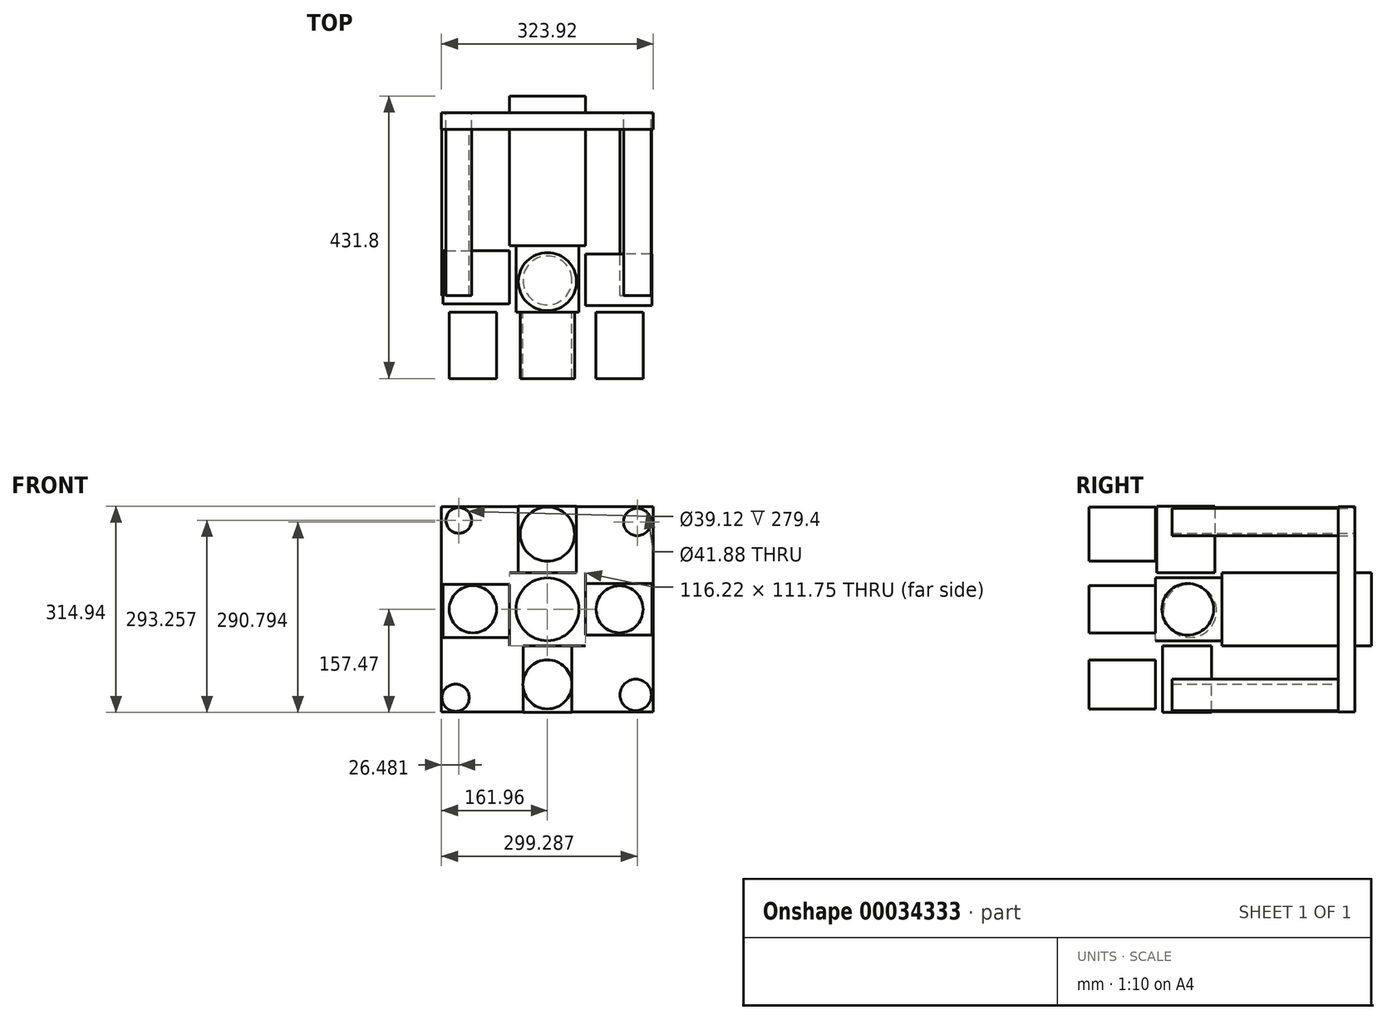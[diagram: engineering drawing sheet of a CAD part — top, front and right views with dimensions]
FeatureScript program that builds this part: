
annotation { "Feature Type Name" : "Feature", "Feature Type Description" : "" }
export const myFeature = defineFeature(function(context is Context, id is Id, definition is map)
    precondition{}
    {
        {
            var Q0;
            Q0=qCreatedBy(makeId("Front.planeOp"),FACE);
            var sketch = newSketch(context, id + "F0", { "sketchPlane" : qUnion([Q0])});
            skLineSegment(sketch, "E0.rect.bottom", {"start": v(58.7, -59.15) * mm, "end": v(-58.7, -59.15) * mm});
            skLineSegment(sketch, "E0.rect.top", {"start": v(58.7, 59.15) * mm, "end": v(-58.7, 59.15) * mm});
            skLineSegment(sketch, "E0.rect.left", {"start": v(58.7, -59.15) * mm, "end": v(58.7, 59.15) * mm});
            skLineSegment(sketch, "E0.rect.right", {"start": v(-58.7, -59.15) * mm, "end": v(-58.7, 59.15) * mm});
            skPoint(sketch, "E0.rect.middle", {"position": v(0, 0) * mm});
            skSolve(sketch);
        }
        {
            var Q0;
            Q0=makeQuery(id+"F0.imprint","IMPRINT",FACE,{"disambiguationData":[TD([[makeQuery(id+"F0.imprint","IMPRINT",EDGE,{"derivedFrom":sQuery(id+"F0.wireOp",EDGE,"E0.rect.bottom")}),-1.0]])]});
            extrude(context, id + "F1", {"entities" : qUnion([Q0]), "depth" : 50.8 * mm});
        }
        {
            var Q0;
            Q0=makeQuery(id+"F1.opExtrude","CAP_FACE",FACE,{"disambiguationData":[OSD([sQuery(id+"F0.wireOp",EDGE,"E0.rect.bottom"),sQuery(id+"F0.wireOp",EDGE,"E0.rect.top"),sQuery(id+"F0.wireOp",EDGE,"E0.rect.left"),sQuery(id+"F0.wireOp",EDGE,"E0.rect.right")])],"isStart":true});
            var sketch = newSketch(context, id + "F2", { "sketchPlane" : qUnion([Q0])});
            skCircle(sketch, "E1", {"center": v(0, 0) * mm, "radius": 46.9 * mm});
            skSolve(sketch);
        }
        {
            var Q0;
            Q0=makeQuery(id+"F2.imprint","IMPRINT",FACE,{"disambiguationData":[TD([[makeQuery(id+"F2.imprint","IMPRINT",EDGE,{"derivedFrom":sQuery(id+"F2.wireOp",EDGE,"E1")}),1.0]])]});
            extrude(context, id + "F3", {"entities" : qUnion([Q0]), "operationType" : NewBodyOperationType.ADD, "oppositeDirection" : true, "depth" : 50.8 * mm});
        }
        {
            var Q0;
            Q0=makeQuery(id+"F1.opExtrude","CAP_FACE",FACE,{"disambiguationData":[OSD([sQuery(id+"F0.wireOp",EDGE,"E0.rect.bottom"),sQuery(id+"F0.wireOp",EDGE,"E0.rect.top"),sQuery(id+"F0.wireOp",EDGE,"E0.rect.left"),sQuery(id+"F0.wireOp",EDGE,"E0.rect.right")])],"isStart":false});
            var sketch = newSketch(context, id + "F4", { "sketchPlane" : qUnion([Q0])});
            skCircle(sketch, "E2", {"center": v(0, 0) * mm, "radius": 42.26 * mm});
            skSolve(sketch);
        }
        {
            var Q0;
            Q0=makeQuery(id+"F4.imprint","IMPRINT",FACE,{"disambiguationData":[TD([[makeQuery(id+"F4.imprint","IMPRINT",EDGE,{"derivedFrom":sQuery(id+"F4.wireOp",EDGE,"E2")}),1.0]])]});
            extrude(context, id + "F5", {"entities" : qUnion([Q0]), "operationType" : NewBodyOperationType.ADD, "depth" : 50.8 * mm});
        }
        {
            var Q0;
            Q0=makeQuery(id+"F1.opExtrude","SWEPT_BODY",BODY,{"disambiguationData":[OSD([sQuery(id+"F0.wireOp",EDGE,"E0.rect.bottom"),sQuery(id+"F0.wireOp",EDGE,"E0.rect.top"),sQuery(id+"F0.wireOp",EDGE,"E0.rect.left"),sQuery(id+"F0.wireOp",EDGE,"E0.rect.right")])]});
            deleteBodies(context, id + "F6", {"entities" : qUnion([Q0])});
        }
        {
            var Q0;
            Q0=qCreatedBy(makeId("Front.planeOp"),FACE);
            var sketch = newSketch(context, id + "F7", { "sketchPlane" : qUnion([Q0])});
            skLineSegment(sketch, "E3.rect.bottom", {"start": v(27.41, -56.77) * mm, "end": v(-27.41, -56.77) * mm});
            skLineSegment(sketch, "E3.rect.top", {"start": v(27.41, 56.77) * mm, "end": v(-27.41, 56.77) * mm});
            skLineSegment(sketch, "E3.rect.left", {"start": v(27.41, -56.77) * mm, "end": v(27.41, 56.77) * mm});
            skLineSegment(sketch, "E3.rect.right", {"start": v(-27.41, -56.77) * mm, "end": v(-27.41, 56.77) * mm});
            skPoint(sketch, "E3.rect.middle", {"position": v(0, 0) * mm});
            skSolve(sketch);
        }
        {
            var Q0;
            Q0=makeQuery(id+"F7.imprint","IMPRINT",FACE,{"disambiguationData":[TD([[makeQuery(id+"F7.imprint","IMPRINT",EDGE,{"derivedFrom":sQuery(id+"F7.wireOp",EDGE,"E3.rect.bottom")}),-1.0]])]});
            extrude(context, id + "F8", {"entities" : qUnion([Q0]), "depth" : 50.8 * mm});
        }
        {
            var Q0;
            Q0=makeQuery(id+"F8.opExtrude","SWEPT_FACE",FACE,{"disambiguationData":[OSD([sQuery(id+"F7.wireOp",EDGE,"E3.rect.left")])]});
            var sketch = newSketch(context, id + "F9", { "sketchPlane" : qUnion([Q0])});
            skSolve(sketch);
        }
        {
            var Q0;
            {var subQ0=sQuery(id+"F7.wireOp",EDGE,"E3.rect.left");Q0=makeQuery(id+"F9.imprint","IMPRINT",FACE,{"disambiguationData":[TD([[makeQuery(id+"F9.imprint","IMPRINT",EDGE,{"derivedFrom":makeQuery(id+"F8.opExtrude","CAP_EDGE",EDGE,{"disambiguationData":[OSD([subQ0])],"isStart":true})}),1.0]])]});}
            extrude(context, id + "F10", {"entities" : qUnion([Q0]), "operationType" : NewBodyOperationType.ADD, "depth" : 25.4 * mm});
        }
        {
            var Q0;
            Q0=makeQuery(id+"F8.opExtrude","SWEPT_BODY",BODY,{"disambiguationData":[OSD([sQuery(id+"F7.wireOp",EDGE,"E3.rect.bottom"),sQuery(id+"F7.wireOp",EDGE,"E3.rect.top"),sQuery(id+"F7.wireOp",EDGE,"E3.rect.left"),sQuery(id+"F7.wireOp",EDGE,"E3.rect.right")])]});
            deleteBodies(context, id + "F11", {"entities" : qUnion([Q0])});
        }
        {
            var Q0;
            Q0=qCreatedBy(makeId("Front.planeOp"),FACE);
            var sketch = newSketch(context, id + "F12", { "sketchPlane" : qUnion([Q0])});
            skLineSegment(sketch, "E4.rect.bottom", {"start": v(58.1, -55.87) * mm, "end": v(-58.1, -55.87) * mm});
            skLineSegment(sketch, "E4.rect.top", {"start": v(58.1, 55.87) * mm, "end": v(-58.1, 55.87) * mm});
            skLineSegment(sketch, "E4.rect.left", {"start": v(58.1, -55.87) * mm, "end": v(58.1, 55.87) * mm});
            skLineSegment(sketch, "E4.rect.right", {"start": v(-58.1, -55.87) * mm, "end": v(-58.1, 55.87) * mm});
            skPoint(sketch, "E4.rect.middle", {"position": v(0, 0) * mm});
            skSolve(sketch);
        }
        {
            var Q0;
            Q0=makeQuery(id+"F12.imprint","IMPRINT",FACE,{"disambiguationData":[TD([[makeQuery(id+"F12.imprint","IMPRINT",EDGE,{"derivedFrom":sQuery(id+"F12.wireOp",EDGE,"E4.rect.bottom")}),-1.0]])]});
            var sketch = newSketch(context, id + "F13", { "sketchPlane" : qUnion([Q0])});
            skCircle(sketch, "E5", {"center": v(0, 0) * mm, "radius": 40.06 * mm});
            skSolve(sketch);
        }
        {
            var Q0;
            Q0=makeQuery(id+"F12.imprint","IMPRINT",FACE,{"disambiguationData":[TD([[makeQuery(id+"F12.imprint","IMPRINT",EDGE,{"derivedFrom":sQuery(id+"F12.wireOp",EDGE,"E4.rect.bottom")}),-1.0]])]});
            extrude(context, id + "F14", {"entities" : qUnion([Q0]), "depth" : 101.6 * mm});
        }
        {
            var Q0;
            Q0=makeQuery(id+"F13.imprint","IMPRINT",FACE,{"disambiguationData":[TD([[makeQuery(id+"F13.imprint","IMPRINT",EDGE,{"derivedFrom":sQuery(id+"F13.wireOp",EDGE,"E5")}),1.0]])]});
            extrude(context, id + "F15", {"entities" : qUnion([Q0]), "operationType" : NewBodyOperationType.ADD, "depth" : 25.4 * mm});
        }
        {
            var Q0;
            Q0=makeQuery(id+"F14.opExtrude","CAP_FACE",FACE,{"disambiguationData":[OSD([sQuery(id+"F12.wireOp",EDGE,"E4.rect.bottom"),sQuery(id+"F12.wireOp",EDGE,"E4.rect.top"),sQuery(id+"F12.wireOp",EDGE,"E4.rect.left"),sQuery(id+"F12.wireOp",EDGE,"E4.rect.right")])],"isStart":false});
            var sketch = newSketch(context, id + "F16", { "sketchPlane" : qUnion([Q0])});
            skCircle(sketch, "E6", {"center": v(0, 0) * mm, "radius": 48.05 * mm});
            skSolve(sketch);
        }
        {
            var Q0;
            Q0=makeQuery(id+"F16.imprint","IMPRINT",FACE,{"disambiguationData":[TD([[makeQuery(id+"F16.imprint","IMPRINT",EDGE,{"derivedFrom":sQuery(id+"F16.wireOp",EDGE,"E6")}),1.0]])]});
            extrude(context, id + "F17", {"entities" : qUnion([Q0]), "operationType" : NewBodyOperationType.ADD, "depth" : 101.6 * mm});
        }
        {
            var Q0;
            Q0=makeQuery(id+"F14.opExtrude","SWEPT_FACE",FACE,{"disambiguationData":[OSD([sQuery(id+"F12.wireOp",EDGE,"E4.rect.right")])]});
            var sketch = newSketch(context, id + "F18", { "sketchPlane" : qUnion([Q0])});
            skCircle(sketch, "E7", {"center": v(150.17, -2.53) * mm, "radius": 40.58 * mm});
            skSolve(sketch);
        }
        {
            var Q0;
            Q0=makeQuery(id+"F18.imprint","IMPRINT",FACE,{"disambiguationData":[TD([[makeQuery(id+"F18.imprint","IMPRINT",EDGE,{"derivedFrom":sQuery(id+"F18.wireOp",EDGE,"E7")}),1.0]])]});
            extrude(context, id + "F19", {"entities" : qUnion([Q0]), "depth" : 101.6 * mm});
        }
        {
            var Q0;
            Q0=makeQuery(id+"F14.opExtrude","SWEPT_FACE",FACE,{"disambiguationData":[OSD([sQuery(id+"F12.wireOp",EDGE,"E4.rect.top")])]});
            var sketch = newSketch(context, id + "F20", { "sketchPlane" : qUnion([Q0])});
            skCircle(sketch, "E8", {"center": v(0, -156.63) * mm, "radius": 44.41 * mm});
            skSolve(sketch);
        }
        {
            var Q0;
            Q0=makeQuery(id+"F20.imprint","IMPRINT",FACE,{"disambiguationData":[TD([[makeQuery(id+"F20.imprint","IMPRINT",EDGE,{"derivedFrom":sQuery(id+"F20.wireOp",EDGE,"E8")}),1.0]])]});
            extrude(context, id + "F21", {"entities" : qUnion([Q0]), "depth" : 101.6 * mm});
        }
        {
            var Q0;
            Q0=makeQuery(id+"F14.opExtrude","SWEPT_FACE",FACE,{"disambiguationData":[OSD([sQuery(id+"F12.wireOp",EDGE,"E4.rect.left")])]});
            var sketch = newSketch(context, id + "F22", { "sketchPlane" : qUnion([Q0])});
            skCircle(sketch, "E9", {"center": v(-153.69, 0) * mm, "radius": 39.5 * mm});
            skSolve(sketch);
        }
        {
            var Q0;
            Q0=makeQuery(id+"F22.imprint","IMPRINT",FACE,{"disambiguationData":[TD([[makeQuery(id+"F22.imprint","IMPRINT",EDGE,{"derivedFrom":sQuery(id+"F22.wireOp",EDGE,"E9")}),1.0]])]});
            extrude(context, id + "F23", {"entities" : qUnion([Q0]), "depth" : 101.6 * mm});
        }
        {
            var Q0;
            Q0=makeQuery(id+"F14.opExtrude","SWEPT_FACE",FACE,{"disambiguationData":[OSD([sQuery(id+"F12.wireOp",EDGE,"E4.rect.bottom")])]});
            var sketch = newSketch(context, id + "F24", { "sketchPlane" : qUnion([Q0])});
            skCircle(sketch, "E10", {"center": v(0, 154.64) * mm, "radius": 37.4 * mm});
            skSolve(sketch);
        }
        {
            var Q0;
            Q0=makeQuery(id+"F24.imprint","IMPRINT",FACE,{"disambiguationData":[TD([[makeQuery(id+"F24.imprint","IMPRINT",EDGE,{"derivedFrom":sQuery(id+"F24.wireOp",EDGE,"E10")}),1.0]])]});
            extrude(context, id + "F25", {"entities" : qUnion([Q0]), "depth" : 101.6 * mm});
        }
        {
            var Q0;
            Q0=makeQuery(id+"F14.opExtrude","CAP_FACE",FACE,{"disambiguationData":[OSD([sQuery(id+"F12.wireOp",EDGE,"E4.rect.bottom"),sQuery(id+"F12.wireOp",EDGE,"E4.rect.top"),sQuery(id+"F12.wireOp",EDGE,"E4.rect.left"),sQuery(id+"F12.wireOp",EDGE,"E4.rect.right")])],"isStart":true});
            var sketch = newSketch(context, id + "F26", { "sketchPlane" : qUnion([Q0])});
            skLineSegment(sketch, "E11.rect.bottom", {"start": v(58.1, -55.87) * mm, "end": v(-58.1, -55.87) * mm});
            skLineSegment(sketch, "E11.rect.top", {"start": v(58.1, 55.87) * mm, "end": v(-58.1, 55.87) * mm});
            skLineSegment(sketch, "E11.rect.left", {"start": v(58.1, -55.87) * mm, "end": v(58.1, 55.87) * mm});
            skLineSegment(sketch, "E11.rect.right", {"start": v(-58.1, -55.87) * mm, "end": v(-58.1, 55.87) * mm});
            skPoint(sketch, "E11.rect.middle", {"position": v(0, 0) * mm});
            skSolve(sketch);
        }
        {
            var Q0;
            Q0=makeQuery(id+"F26.imprint","IMPRINT",FACE,{"disambiguationData":[TD([[makeQuery(id+"F26.imprint","IMPRINT",EDGE,{"derivedFrom":sQuery(id+"F26.wireOp",EDGE,"E11.rect.bottom")}),1.0]])]});
            extrude(context, id + "F27", {"entities" : qUnion([Q0]), "operationType" : NewBodyOperationType.ADD, "depth" : 101.6 * mm});
        }
        {
            var Q0;
            Q0=makeQuery(id+"F17.opExtrude","CAP_FACE",FACE,{"disambiguationData":[OSD([sQuery(id+"F16.wireOp",EDGE,"E6")])],"isStart":false});
            var sketch = newSketch(context, id + "F28", { "sketchPlane" : qUnion([Q0])});
            skCircle(sketch, "E12", {"center": v(0, 114.85) * mm, "radius": 41.52 * mm});
            skSolve(sketch);
        }
        {
            var Q0;
            Q0=makeQuery(id+"F28.imprint","IMPRINT",FACE,{"disambiguationData":[TD([[makeQuery(id+"F28.imprint","IMPRINT",EDGE,{"derivedFrom":sQuery(id+"F28.wireOp",EDGE,"E12")}),1.0]])]});
            extrude(context, id + "F29", {"entities" : qUnion([Q0]), "depth" : 101.6 * mm});
        }
        {
            var Q0;
            Q0=makeQuery(id+"F17.opExtrude","CAP_FACE",FACE,{"disambiguationData":[OSD([sQuery(id+"F16.wireOp",EDGE,"E6")])],"isStart":false});
            var sketch = newSketch(context, id + "F30", { "sketchPlane" : qUnion([Q0])});
            skCircle(sketch, "E13", {"center": v(-113.93, 0) * mm, "radius": 36.08 * mm});
            skSolve(sketch);
        }
        {
            var Q0;
            Q0=makeQuery(id+"F30.imprint","IMPRINT",FACE,{"disambiguationData":[TD([[makeQuery(id+"F30.imprint","IMPRINT",EDGE,{"derivedFrom":sQuery(id+"F30.wireOp",EDGE,"E13")}),1.0]])]});
            extrude(context, id + "F31", {"entities" : qUnion([Q0]), "depth" : 101.6 * mm});
        }
        {
            var Q0;
            Q0=makeQuery(id+"F17.opExtrude","CAP_FACE",FACE,{"disambiguationData":[OSD([sQuery(id+"F16.wireOp",EDGE,"E6")])],"isStart":false});
            var sketch = newSketch(context, id + "F32", { "sketchPlane" : qUnion([Q0])});
            skCircle(sketch, "E14", {"center": v(110.23, 0) * mm, "radius": 35.93 * mm});
            skSolve(sketch);
        }
        {
            var Q0;
            Q0=makeQuery(id+"F32.imprint","IMPRINT",FACE,{"disambiguationData":[TD([[makeQuery(id+"F32.imprint","IMPRINT",EDGE,{"derivedFrom":sQuery(id+"F32.wireOp",EDGE,"E14")}),1.0]])]});
            extrude(context, id + "F33", {"entities" : qUnion([Q0]), "depth" : 101.6 * mm});
        }
        {
            var Q0;
            Q0=makeQuery(id+"F17.opExtrude","CAP_FACE",FACE,{"disambiguationData":[OSD([sQuery(id+"F16.wireOp",EDGE,"E6")])],"isStart":false});
            var sketch = newSketch(context, id + "F34", { "sketchPlane" : qUnion([Q0])});
            skCircle(sketch, "E15", {"center": v(0, -114.85) * mm, "radius": 37.46 * mm});
            skSolve(sketch);
        }
        {
            var Q0;
            Q0=makeQuery(id+"F34.imprint","IMPRINT",FACE,{"disambiguationData":[TD([[makeQuery(id+"F34.imprint","IMPRINT",EDGE,{"derivedFrom":sQuery(id+"F34.wireOp",EDGE,"E15")}),1.0]])]});
            extrude(context, id + "F35", {"entities" : qUnion([Q0]), "depth" : 101.6 * mm});
        }
        {
            var Q0;
            Q0=makeQuery(id+"F27.opExtrude","CAP_FACE",FACE,{"disambiguationData":[OSD([sQuery(id+"F26.wireOp",EDGE,"E11.rect.bottom"),sQuery(id+"F26.wireOp",EDGE,"E11.rect.top"),sQuery(id+"F26.wireOp",EDGE,"E11.rect.left"),sQuery(id+"F26.wireOp",EDGE,"E11.rect.right")])],"isStart":false});
            var sketch = newSketch(context, id + "F36", { "sketchPlane" : qUnion([Q0])});
            skLineSegment(sketch, "E16.rect.bottom", {"start": v(161.96, -156.73) * mm, "end": v(-161.96, -156.73) * mm});
            skLineSegment(sketch, "E16.rect.top", {"start": v(161.96, 156.73) * mm, "end": v(-161.96, 156.73) * mm});
            skLineSegment(sketch, "E16.rect.left", {"start": v(161.96, -156.73) * mm, "end": v(161.96, 156.73) * mm});
            skLineSegment(sketch, "E16.rect.right", {"start": v(-161.96, -156.73) * mm, "end": v(-161.96, 156.73) * mm});
            skPoint(sketch, "E16.rect.middle", {"position": v(0, 0) * mm});
            skSolve(sketch);
        }
        {
            var Q0;
            Q0=makeQuery(id+"F36.imprint","IMPRINT",FACE,{"disambiguationData":[TD([[makeQuery(id+"F36.imprint","IMPRINT",EDGE,{"derivedFrom":sQuery(id+"F36.wireOp",EDGE,"E16.rect.bottom")}),-1.0]])]});
            extrude(context, id + "F37", {"entities" : qUnion([Q0]), "depth" : 25.4 * mm});
        }
        {
            var Q0;
            Q0=makeQuery(id+"F27.opExtrude","CAP_FACE",FACE,{"disambiguationData":[OSD([sQuery(id+"F26.wireOp",EDGE,"E11.rect.bottom"),sQuery(id+"F26.wireOp",EDGE,"E11.rect.top"),sQuery(id+"F26.wireOp",EDGE,"E11.rect.left"),sQuery(id+"F26.wireOp",EDGE,"E11.rect.right")])],"isStart":false});
            var sketch = newSketch(context, id + "F38", { "sketchPlane" : qUnion([Q0])});
            skLineSegment(sketch, "E17.rect.bottom", {"start": v(58.1, -55.87) * mm, "end": v(-58.1, -55.87) * mm});
            skLineSegment(sketch, "E17.rect.top", {"start": v(58.1, 55.87) * mm, "end": v(-58.1, 55.87) * mm});
            skLineSegment(sketch, "E17.rect.left", {"start": v(58.1, -55.87) * mm, "end": v(58.1, 55.87) * mm});
            skLineSegment(sketch, "E17.rect.right", {"start": v(-58.1, -55.87) * mm, "end": v(-58.1, 55.87) * mm});
            skPoint(sketch, "E17.rect.middle", {"position": v(0, 0) * mm});
            skSolve(sketch);
        }
        {
            var Q0;
            Q0=makeQuery(id+"F38.imprint","IMPRINT",FACE,{"disambiguationData":[TD([[makeQuery(id+"F38.imprint","IMPRINT",EDGE,{"derivedFrom":sQuery(id+"F38.wireOp",EDGE,"E17.rect.bottom")}),1.0]])]});
            extrude(context, id + "F39", {"entities" : qUnion([Q0]), "depth" : 25.4 * mm});
        }
        {
            var Q0;
            Q0=makeQuery(id+"F37.opExtrude","CAP_FACE",FACE,{"disambiguationData":[OSD([sQuery(id+"F26.wireOp",EDGE,"E11.rect.bottom"),sQuery(id+"F26.wireOp",EDGE,"E11.rect.top"),sQuery(id+"F26.wireOp",EDGE,"E11.rect.left"),sQuery(id+"F26.wireOp",EDGE,"E11.rect.right"),sQuery(id+"F36.wireOp",EDGE,"E16.rect.bottom"),sQuery(id+"F36.wireOp",EDGE,"E16.rect.top"),sQuery(id+"F36.wireOp",EDGE,"E16.rect.left"),sQuery(id+"F36.wireOp",EDGE,"E16.rect.right")])],"isStart":true});
            var sketch = newSketch(context, id + "F40", { "sketchPlane" : qUnion([Q0])});
            skCircle(sketch, "E18", {"center": v(-135.48, 135.79) * mm, "radius": 19.56 * mm});
            skCircle(sketch, "E19", {"center": v(138.56, 136.4) * mm, "radius": 18.62 * mm});
            skCircle(sketch, "E20", {"center": v(134.25, -133.94) * mm, "radius": 23.12 * mm});
            skCircle(sketch, "E21", {"center": v(-133.02, -135.17) * mm, "radius": 20.66 * mm});
            skSolve(sketch);
        }
        {
            var Q0;
            Q0=makeQuery(id+"F40.imprint","IMPRINT",FACE,{"disambiguationData":[TD([[makeQuery(id+"F40.imprint","IMPRINT",EDGE,{"derivedFrom":sQuery(id+"F40.wireOp",EDGE,"E18")}),1.0]])]});
            extrude(context, id + "F41", {"entities" : qUnion([Q0]), "operationType" : NewBodyOperationType.ADD, "depth" : 254 * mm});
        }
        {
            var Q0;
            Q0=makeQuery(id+"F37.opExtrude","CAP_FACE",FACE,{"disambiguationData":[OSD([sQuery(id+"F26.wireOp",EDGE,"E11.rect.bottom"),sQuery(id+"F26.wireOp",EDGE,"E11.rect.top"),sQuery(id+"F26.wireOp",EDGE,"E11.rect.left"),sQuery(id+"F26.wireOp",EDGE,"E11.rect.right"),sQuery(id+"F36.wireOp",EDGE,"E16.rect.bottom"),sQuery(id+"F36.wireOp",EDGE,"E16.rect.top"),sQuery(id+"F36.wireOp",EDGE,"E16.rect.left"),sQuery(id+"F36.wireOp",EDGE,"E16.rect.right")])],"isStart":true});
            var sketch = newSketch(context, id + "F42", { "sketchPlane" : qUnion([Q0])});
            skCircle(sketch, "E22", {"center": v(137.33, 133.32) * mm, "radius": 20.94 * mm});
            skSolve(sketch);
        }
        {
            var Q0;
            Q0=makeQuery(id+"F37.opExtrude","SWEPT_BODY",BODY,{"disambiguationData":[OSD([sQuery(id+"F26.wireOp",EDGE,"E11.rect.bottom"),sQuery(id+"F26.wireOp",EDGE,"E11.rect.top"),sQuery(id+"F26.wireOp",EDGE,"E11.rect.left"),sQuery(id+"F26.wireOp",EDGE,"E11.rect.right"),sQuery(id+"F36.wireOp",EDGE,"E16.rect.bottom"),sQuery(id+"F36.wireOp",EDGE,"E16.rect.top"),sQuery(id+"F36.wireOp",EDGE,"E16.rect.left"),sQuery(id+"F36.wireOp",EDGE,"E16.rect.right")])]});
            deleteBodies(context, id + "F43", {"entities" : qUnion([Q0])});
        }
        {
            var Q0;
            Q0=makeQuery(id+"F42.imprint","IMPRINT",FACE,{"disambiguationData":[TD([[makeQuery(id+"F42.imprint","IMPRINT",EDGE,{"derivedFrom":sQuery(id+"F42.wireOp",EDGE,"E22")}),-1.0]])]});
            extrude(context, id + "F44", {"entities" : qUnion([Q0]), "operationType" : NewBodyOperationType.ADD, "depth" : 25.4 * mm});
        }
        {
            var Q0;
            Q0=makeQuery(id+"F44.opExtrude","CAP_FACE",FACE,{"disambiguationData":[OSD([sQuery(id+"F26.wireOp",EDGE,"E11.rect.bottom"),sQuery(id+"F26.wireOp",EDGE,"E11.rect.top"),sQuery(id+"F26.wireOp",EDGE,"E11.rect.left"),sQuery(id+"F26.wireOp",EDGE,"E11.rect.right"),sQuery(id+"F36.wireOp",EDGE,"E16.rect.bottom"),sQuery(id+"F36.wireOp",EDGE,"E16.rect.top"),sQuery(id+"F36.wireOp",EDGE,"E16.rect.left"),sQuery(id+"F36.wireOp",EDGE,"E16.rect.right"),sQuery(id+"F40.wireOp",EDGE,"E18"),sQuery(id+"F42.wireOp",EDGE,"E22")])],"isStart":false});
            var sketch = newSketch(context, id + "F45", { "sketchPlane" : qUnion([Q0])});
            skCircle(sketch, "E23", {"center": v(-135.48, 135.79) * mm, "radius": 19.6 * mm});
            skSolve(sketch);
        }
        {
            var Q0;
            Q0=makeQuery(id+"F45.imprint","IMPRINT",FACE,{"disambiguationData":[TD([[makeQuery(id+"F45.imprint","IMPRINT",EDGE,{"derivedFrom":sQuery(id+"F45.wireOp",EDGE,"E23")}),1.0]])]});
            extrude(context, id + "F46", {"entities" : qUnion([Q0]), "operationType" : NewBodyOperationType.ADD, "depth" : 254 * mm});
        }
        {
            var Q0;
            Q0=makeQuery(id+"F44.opExtrude","CAP_FACE",FACE,{"disambiguationData":[OSD([sQuery(id+"F26.wireOp",EDGE,"E11.rect.bottom"),sQuery(id+"F26.wireOp",EDGE,"E11.rect.top"),sQuery(id+"F26.wireOp",EDGE,"E11.rect.left"),sQuery(id+"F26.wireOp",EDGE,"E11.rect.right"),sQuery(id+"F36.wireOp",EDGE,"E16.rect.bottom"),sQuery(id+"F36.wireOp",EDGE,"E16.rect.top"),sQuery(id+"F36.wireOp",EDGE,"E16.rect.left"),sQuery(id+"F36.wireOp",EDGE,"E16.rect.right"),sQuery(id+"F40.wireOp",EDGE,"E18"),sQuery(id+"F42.wireOp",EDGE,"E22")])],"isStart":false});
            var sketch = newSketch(context, id + "F47", { "sketchPlane" : qUnion([Q0])});
            skCircle(sketch, "E24", {"center": v(137.33, 133.32) * mm, "radius": 21.35 * mm});
            skSolve(sketch);
        }
        {
            var Q0;
            Q0=makeQuery(id+"F47.imprint","IMPRINT",FACE,{"disambiguationData":[TD([[makeQuery(id+"F47.imprint","IMPRINT",EDGE,{"derivedFrom":makeQuery(id+"F44.opExtrude","CAP_EDGE",EDGE,{"disambiguationData":[OSD([sQuery(id+"F42.wireOp",EDGE,"E22")])],"isStart":false})}),1.0]])]});
            extrude(context, id + "F48", {"entities" : qUnion([Q0]), "depth" : 254 * mm});
        }
        {
            var Q0;
            Q0=makeQuery(id+"F44.opExtrude","CAP_FACE",FACE,{"disambiguationData":[OSD([sQuery(id+"F26.wireOp",EDGE,"E11.rect.bottom"),sQuery(id+"F26.wireOp",EDGE,"E11.rect.top"),sQuery(id+"F26.wireOp",EDGE,"E11.rect.left"),sQuery(id+"F26.wireOp",EDGE,"E11.rect.right"),sQuery(id+"F36.wireOp",EDGE,"E16.rect.bottom"),sQuery(id+"F36.wireOp",EDGE,"E16.rect.top"),sQuery(id+"F36.wireOp",EDGE,"E16.rect.left"),sQuery(id+"F36.wireOp",EDGE,"E16.rect.right"),sQuery(id+"F40.wireOp",EDGE,"E18"),sQuery(id+"F42.wireOp",EDGE,"E22")])],"isStart":false});
            var sketch = newSketch(context, id + "F49", { "sketchPlane" : qUnion([Q0])});
            skCircle(sketch, "E25", {"center": v(-140.4, -135.17) * mm, "radius": 20.84 * mm});
            skSolve(sketch);
        }
        {
            var Q0;
            Q0=makeQuery(id+"F49.imprint","IMPRINT",FACE,{"disambiguationData":[TD([[makeQuery(id+"F49.imprint","IMPRINT",EDGE,{"derivedFrom":sQuery(id+"F49.wireOp",EDGE,"E25")}),1.0]])]});
            extrude(context, id + "F50", {"entities" : qUnion([Q0]), "operationType" : NewBodyOperationType.ADD, "depth" : 254 * mm});
        }
        {
            var Q0;
            Q0=makeQuery(id+"F44.opExtrude","CAP_FACE",FACE,{"disambiguationData":[OSD([sQuery(id+"F26.wireOp",EDGE,"E11.rect.bottom"),sQuery(id+"F26.wireOp",EDGE,"E11.rect.top"),sQuery(id+"F26.wireOp",EDGE,"E11.rect.left"),sQuery(id+"F26.wireOp",EDGE,"E11.rect.right"),sQuery(id+"F36.wireOp",EDGE,"E16.rect.bottom"),sQuery(id+"F36.wireOp",EDGE,"E16.rect.top"),sQuery(id+"F36.wireOp",EDGE,"E16.rect.left"),sQuery(id+"F36.wireOp",EDGE,"E16.rect.right"),sQuery(id+"F40.wireOp",EDGE,"E18"),sQuery(id+"F42.wireOp",EDGE,"E22")])],"isStart":false});
            var sketch = newSketch(context, id + "F51", { "sketchPlane" : qUnion([Q0])});
            skCircle(sketch, "E26", {"center": v(134.86, -130.86) * mm, "radius": 23.99 * mm});
            skSolve(sketch);
        }
        {
            var Q0;
            Q0=makeQuery(id+"F51.imprint","IMPRINT",FACE,{"disambiguationData":[TD([[makeQuery(id+"F51.imprint","IMPRINT",EDGE,{"derivedFrom":sQuery(id+"F51.wireOp",EDGE,"E26")}),1.0]])]});
            extrude(context, id + "F52", {"entities" : qUnion([Q0]), "operationType" : NewBodyOperationType.ADD, "depth" : 254 * mm});
        }
    });
